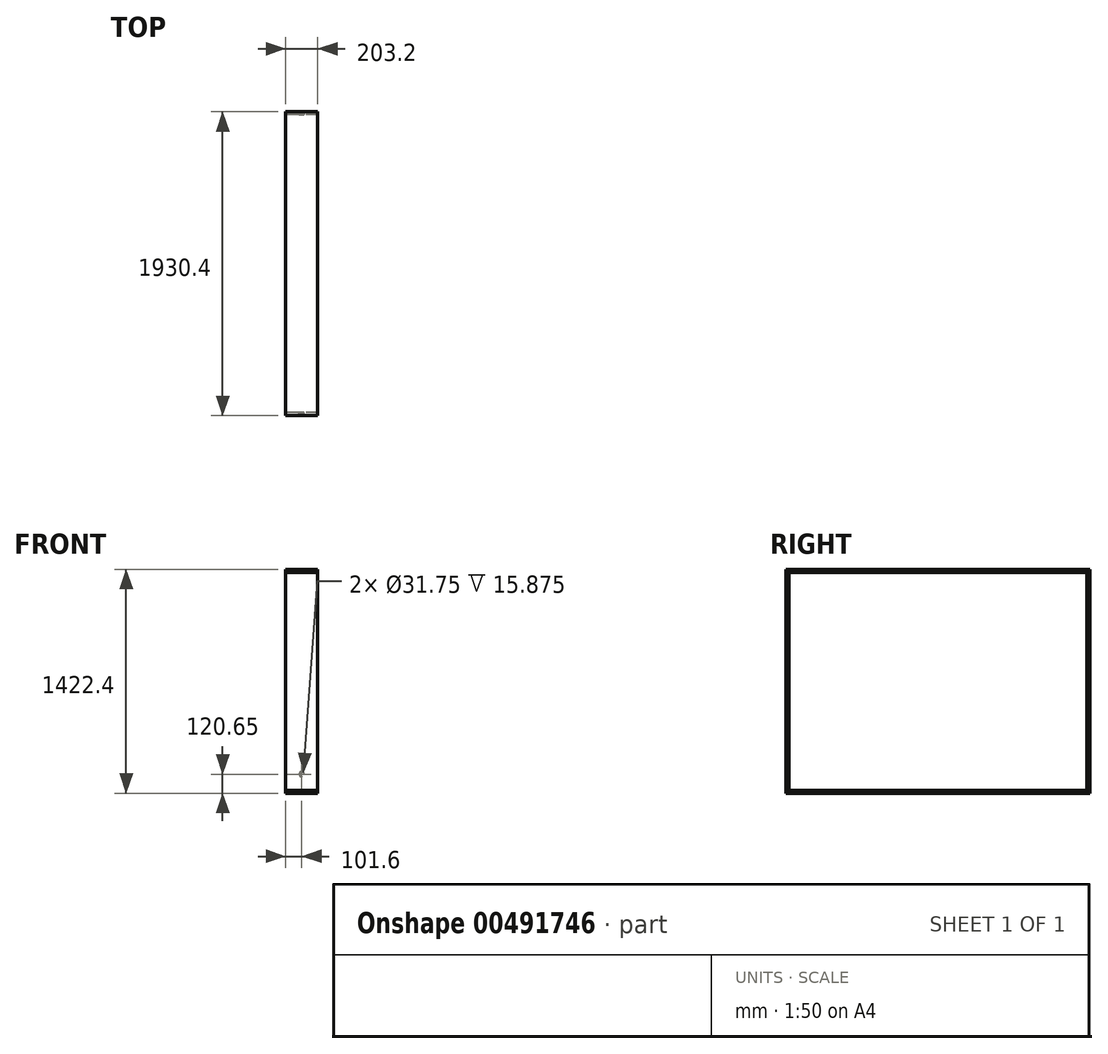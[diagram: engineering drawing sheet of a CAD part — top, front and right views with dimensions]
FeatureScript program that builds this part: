
annotation { "Feature Type Name" : "Feature", "Feature Type Description" : "" }
export const myFeature = defineFeature(function(context is Context, id is Id, definition is map)
    precondition{}
    {
        {
            var Q0;
            Q0=qCreatedBy(makeId("Right.planeOp"),FACE);
            var sketch = newSketch(context, id + "F0", { "sketchPlane" : qUnion([Q0])});
            skLineSegment(sketch, "E0.bottom", {"start": v(-965.2, 0) * mm, "end": v(965.2, 0) * mm});
            skLineSegment(sketch, "E0.top", {"start": v(-965.2, 1422.4) * mm, "end": v(965.2, 1422.4) * mm});
            skLineSegment(sketch, "E0.left", {"start": v(-965.2, 0) * mm, "end": v(-965.2, 19.05) * mm});
            skLineSegment(sketch, "E0.right", {"start": v(965.2, 0) * mm, "end": v(965.2, 19.05) * mm});
            skPoint(sketch, "E0.middle", {"position": v(0, 711.2) * mm});
            skLineSegment(sketch, "E1", {"start": v(-965.2, 1403.35) * mm, "end": v(965.2, 1403.35) * mm});
            skLineSegment(sketch, "E2", {"start": v(-965.2, 19.05) * mm, "end": v(965.2, 19.05) * mm});
            skLineSegment(sketch, "E3.trimOffspring", {"start": v(-965.2, 1403.35) * mm, "end": v(-965.2, 1422.4) * mm});
            skLineSegment(sketch, "E4.trimOffspring", {"start": v(965.2, 1403.35) * mm, "end": v(965.2, 1422.4) * mm});
            skSolve(sketch);
        }
        {
            var Q0;
            Q0 = qSketchRegion(id + "F0", true);
            extrude(context, id + "F1", {"entities" : qUnion([Q0]), "depth" : 203.2 * mm});
        }
        {
            var Q0;
            Q0=qCreatedBy(makeId("Right.planeOp"),FACE);
            var sketch = newSketch(context, id + "F2", { "sketchPlane" : qUnion([Q0])});
            skLineSegment(sketch, "E5.bottom", {"start": v(-965.2, 1403.35) * mm, "end": v(-946.15, 1403.35) * mm});
            skLineSegment(sketch, "E5.top", {"start": v(-965.2, 19.05) * mm, "end": v(-946.15, 19.05) * mm});
            skLineSegment(sketch, "E5.left", {"start": v(-965.2, 1403.35) * mm, "end": v(-965.2, 19.05) * mm});
            skLineSegment(sketch, "E5.right", {"start": v(-946.15, 1403.35) * mm, "end": v(-946.15, 19.05) * mm});
            skLineSegment(sketch, "E6.bottom", {"start": v(946.15, 1403.35) * mm, "end": v(965.2, 1403.35) * mm});
            skLineSegment(sketch, "E6.top", {"start": v(946.15, 19.05) * mm, "end": v(965.2, 19.05) * mm});
            skLineSegment(sketch, "E6.left", {"start": v(946.15, 1403.35) * mm, "end": v(946.15, 19.05) * mm});
            skLineSegment(sketch, "E6.right", {"start": v(965.2, 1403.35) * mm, "end": v(965.2, 19.05) * mm});
            skSolve(sketch);
        }
        {
            var Q0;
            Q0 = qSketchRegion(id + "F2", true);
            var Q1;
            Q1=makeQuery(id+"F1.opExtrude","CAP_FACE",FACE,{"disambiguationData":[OSD([sQuery(id+"F0.wireOp",EDGE,"E0.top"),sQuery(id+"F0.wireOp",EDGE,"E1"),sQuery(id+"F0.wireOp",EDGE,"E3.trimOffspring"),sQuery(id+"F0.wireOp",EDGE,"E4.trimOffspring")])],"isStart":false});
            extrude(context, id + "F3", {"entities" : qUnion([Q0]), "endBound" : BoundingType.UP_TO_SURFACE, "endBoundEntityFace" : qUnion([Q1]), "depth" : 25.4 * mm});
        }
        {
            var Q0;
            Q0=makeQuery(id+"F3.opExtrude","SWEPT_FACE",FACE,{"disambiguationData":[OSD([sQuery(id+"F2.wireOp",EDGE,"E5.right")])]});
            var sketch = newSketch(context, id + "F4", { "sketchPlane" : qUnion([Q0])});
            skCircle(sketch, "E7", {"center": v(-101.6, 120.65) * mm, "radius": 15.88 * mm});
            skSolve(sketch);
        }
        {
            var Q0;
            Q0 = qSketchRegion(id + "F4", true);
            extrude(context, id + "F5", {"entities" : qUnion([Q0]), "operationType" : NewBodyOperationType.REMOVE, "oppositeDirection" : true, "depth" : 15.88 * mm});
        }
        {
            var Q0;
            Q0=makeQuery(id+"F3.opExtrude","SWEPT_FACE",FACE,{"disambiguationData":[OSD([sQuery(id+"F2.wireOp",EDGE,"E6.left")])]});
            var sketch = newSketch(context, id + "F6", { "sketchPlane" : qUnion([Q0])});
            skCircle(sketch, "E8.0", {"center": v(101.6, 120.65) * mm, "radius": 15.88 * mm});
            skSolve(sketch);
        }
        {
            var Q0;
            Q0 = qSketchRegion(id + "F6", true);
            extrude(context, id + "F7", {"entities" : qUnion([Q0]), "operationType" : NewBodyOperationType.REMOVE, "oppositeDirection" : true, "depth" : 15.88 * mm});
        }
    });
